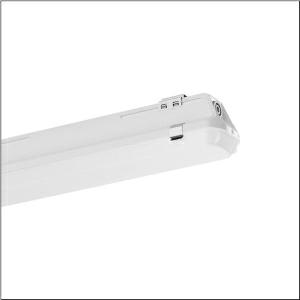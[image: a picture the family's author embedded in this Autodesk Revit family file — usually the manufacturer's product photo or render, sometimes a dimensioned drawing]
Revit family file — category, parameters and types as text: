
# Revit family: monsun_r__11_emergency_51fp10dp467h3h_d298
name_source: partatom
category: Lighting Fixtures
units: mm (PartAtom-declared; Revit-internal decimal feet)

## family parameters
Cut with Voids When Loaded = No
Host = Face
Light Source = No
Part Type = Normal
Room Calculation Point = No
Round Connector Dimension = Use Diameter
Shared = No

## types (1)
- --- (1 x LED, 870 lm, 5 W, 4000K)
    Apparent Load = 5 VA
    CIE Flux Codes = 47 77 93 94 100
    Color Rendering = 80
    Color Temperature = 4000K
    Default Elevation = 1800 mm
    Description = Monsun® 11 emergency, damp-proof luminaire, chain hanger, primary optical cover: enclosure, of PMMA, light emission: direct distribution, primary light characteristic: symmetric, installation type: suspended mounting, surface-mounted, horizontal mounting, vertical mounting, LED, rated luminous flux: 6.050lm, luminous efficacy: 175lm/W, light colour: 840, colour temperature: 4000K, control gear: ECG DALI, with terminal, 5+3-pole, max. 2.5mm², mains connection: 220..240V, AC, 50/60Hz, rated input power: 35W, control gear: single battery element, battery: NiCd, 4,5Ah, mains connection: 230V, 50Hz, luminaire housing, of glass-fibre reinforced polyester, uncoated, bright grey, incl. chain hanger, length: 1.590mm, width: 90mm, height: 88mm, clip for enclosure, of stainless steel (V2A), ceiling mounting element, of stainless steel (V2A), chain hanger, of stainless steel (V2A), protection rating (complete): IP66, insulation class (complete): insulation class I (protective earthing), certification: CE, UKCA, protection symbol: D, impact resistance: IK04, permissible operating ambient temperature: +5..+35°C, standard: EN 50419, EN 60598-2-1, EN 60598-2-22, no direct snow, no direct sun, no direct rain, for indoor or canopied outdoor use, corresponds to IFS (International Featured Standards) requirements for safety and quality in the food industry, contact your sales advisor before using the luminaires in applications with unclear chemical exposure, large temperature fluctuations or condensation-forming humidity, LABS conformity tested according to VDMA 24364:2018-05, packaging unit: 1 piece
    Height = 89 mm
    Lamp = 1 x LED
    Lamp Light Flux = 870 lm
    Lamp Power = 5 W
    Lamp count = 1
    Length = 1590 mm
    Luminous efficacy = 174 lm/W
    Manufacturer = Siteco
    ModVariant = No
    Model = 51FP10DP467H3H
    Mounting Place = Ceiling
    Mounting Type = Surface mounted
    Number of Poles = 1
    OnlyDefault = Yes
    Power Factor = 1
    Product Name = Monsun® 11 emergency
    Product group = damp-proof luminaire
    ProductGroupID = 300
    Protection Class = Protection class I
    Protection Degree = IP 66
    RLX_Detail_Level = 1
    RLX_Emergency_Light_Flux = 0 lm
    RLX_Emergency_Type = 0
    RLX_Emergency_Type_DB = No
    RlxData = <blob elided: 92741 chars, md5=3ed142ca>
    Socket = socket
    Standby Power = 0 W
    System Light Flux = 870 lm
    System Power = 5 W
    Type Comments = : emergency light operation: 3 h
    Type Image = l_1319650.jpg
    URL = http://relux.com
    VarID = @adj_171463
    Voltage = 0 V
    Weight = 0.00 kg
    Width = 90 mm

## geometry (parser evidence)
native form markers: Blend x4, Sweep x14
no freeform markers — native parametric forms only
